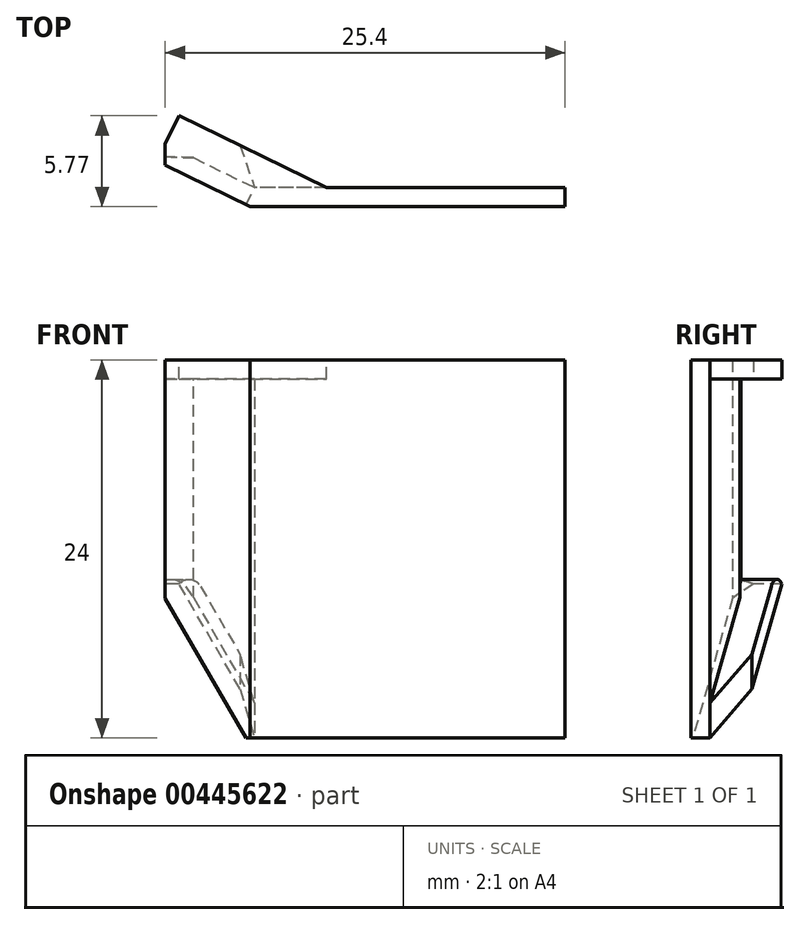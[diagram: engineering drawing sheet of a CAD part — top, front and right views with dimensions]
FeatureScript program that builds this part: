
annotation { "Feature Type Name" : "Feature", "Feature Type Description" : "" }
export const myFeature = defineFeature(function(context is Context, id is Id, definition is map)
    precondition{}
    {
        {
            var Q0;
            Q0=qCreatedBy(makeId("Top.planeOp"),FACE);
            var sketch = newSketch(context, id + "F0", { "sketchPlane" : qUnion([Q0])});
            skLineSegment(sketch, "E0", {"start": v(0, 0) * mm, "end": v(-20, 0) * mm});
            skLineSegment(sketch, "E1", {"start": v(-20, 0) * mm, "end": v(-25.4, 2.63) * mm});
            skLineSegment(sketch, "E2.0", {"start": v(-19.72, 1.2) * mm, "end": v(-25.4, 3.97) * mm});
            skLineSegment(sketch, "E2.1", {"start": v(0, 1.2) * mm, "end": v(-19.72, 1.2) * mm});
            skLineSegment(sketch, "E3", {"start": v(-25.4, 2.63) * mm, "end": v(-25.4, 3.97) * mm});
            skLineSegment(sketch, "E4", {"start": v(0, 0) * mm, "end": v(0, 1.2) * mm});
            skSolve(sketch);
        }
        {
            var Q0;
            Q0 = qSketchRegion(id + "F0", true);
            extrude(context, id + "F1", {"entities" : qUnion([Q0]), "depth" : 24 * mm});
        }
        {
            var Q0;
            Q0=makeQuery(id+"F1.opExtrude","SWEPT_FACE",FACE,{"disambiguationData":[OSD([sQuery(id+"F0.wireOp",EDGE,"E2.0")])]});
            var sketch = newSketch(context, id + "F2", { "sketchPlane" : qUnion([Q0])});
            skLineSegment(sketch, "E5", {"start": v(18.25, 0) * mm, "end": v(24.57, 9.79) * mm});
            skLineSegment(sketch, "E6", {"start": v(24.57, 9.79) * mm, "end": v(24.57, 12) * mm});
            skLineSegment(sketch, "E7", {"start": v(24.57, 12) * mm, "end": v(18.25, 2.21) * mm});
            skLineSegment(sketch, "E8", {"start": v(18.25, 2.21) * mm, "end": v(18.25, 0) * mm});
            skSolve(sketch);
        }
        {
            var Q0;
            Q0 = qSketchRegion(id + "F2", true);
            extrude(context, id + "F3", {"entities" : qUnion([Q0]), "operationType" : NewBodyOperationType.ADD, "depth" : 2 * mm});
        }
        {
            var Q0;
            Q0=makeQuery(id+"F3.opExtrude","CAP_EDGE",EDGE,{"disambiguationData":[OSD([sQuery(id+"F2.wireOp",EDGE,"E8")])],"isStart":false});
            chamfer(context, id + "F4", {"entities" : qUnion([Q0]), "width" : 2 * mm, "tangentPropagation" : true});
        }
        {
            var Q0;
            {var subQ2=sQuery(id+"F0.wireOp",EDGE,"E2.0");Q0=makeQuery(id+"F3.boolean.opBoolean","SPLIT",FACE,{"disambiguationData":[TD([makeQuery(id+"F3.opExtrude","SWEPT_FACE",FACE,{"disambiguationData":[OSD([sQuery(id+"F2.wireOp",EDGE,"E5")])]})])],"derivedFrom":makeQuery(id+"F1.opExtrude","SWEPT_FACE",FACE,{"disambiguationData":[OSD([subQ2])]})});}
            extrude(context, id + "F5", {"entities" : qUnion([Q0]), "operationType" : NewBodyOperationType.REMOVE, "oppositeDirection" : true, "depth" : 25 * mm});
        }
        {
            var Q0;
            Q0=makeQuery(id+"F1.opExtrude","CAP_FACE",FACE,{"disambiguationData":[OSD([sQuery(id+"F0.wireOp",EDGE,"E0"),sQuery(id+"F0.wireOp",EDGE,"E1"),sQuery(id+"F0.wireOp",EDGE,"E2.0"),sQuery(id+"F0.wireOp",EDGE,"E2.1"),sQuery(id+"F0.wireOp",EDGE,"E3"),sQuery(id+"F0.wireOp",EDGE,"E4")])],"isStart":false});
            var sketch = newSketch(context, id + "F6", { "sketchPlane" : qUnion([Q0])});
            skLineSegment(sketch, "E9", {"start": v(-25.4, 3.97) * mm, "end": v(-24.53, 5.77) * mm});
            skLineSegment(sketch, "E10", {"start": v(-24.53, 5.77) * mm, "end": v(-15.16, 1.2) * mm});
            skSolve(sketch);
        }
        {
            var Q0;
            Q0=makeQuery(id+"F6.imprint","IMPRINT",FACE,{"disambiguationData":[TD([[makeQuery(id+"F6.imprint","IMPRINT",EDGE,{"derivedFrom":sQuery(id+"F6.wireOp",EDGE,"E9")}),-1.0]])]});
            extrude(context, id + "F7", {"entities" : qUnion([Q0]), "operationType" : NewBodyOperationType.ADD, "oppositeDirection" : true, "depth" : 1.2 * mm});
        }
        {
            var Q0;
            {var subQ0=sQuery(id+"F0.wireOp",EDGE,"E2.0");var subQ1=sQuery(id+"F0.wireOp",EDGE,"E3");Q0=makeQuery(id+"F7.boolean.opBoolean","SPLIT",EDGE,{"derivedFrom":makeQuery(id+"F3.boolean.opBoolean","SPLIT",EDGE,{"disambiguationData":[TD([makeQuery(id+"F3.opExtrude","SWEPT_FACE",FACE,{"disambiguationData":[OSD([sQuery(id+"F2.wireOp",EDGE,"E7")])]})])],"derivedFrom":makeQuery(id+"F1.opExtrude","SWEPT_EDGE",EDGE,{"disambiguationData":[OSD([subQ0,subQ1])]})})});}
            chamfer(context, id + "F8", {"entities" : qUnion([Q0]), "chamferType" : ChamferType.TWO_OFFSETS, "width1" : 0.8 * mm, "oppositeDirection" : false, "width2" : 2 * mm, "tangentPropagation" : true});
        }
        {
            var Q0;
            Q0=makeQuery(id+"F3.opExtrude","SWEPT_EDGE",EDGE,{"disambiguationData":[OSD([sQuery(id+"F0.wireOp",EDGE,"E2.0"),sQuery(id+"F0.wireOp",EDGE,"E3"),sQuery(id+"F2.wireOp",EDGE,"E6"),sQuery(id+"F2.wireOp",EDGE,"E7")])]});
            fillet(context, id + "F9", {"entities" : qUnion([Q0]), "radius" : 1 * mm, "tangentPropagation" : true, "allowEdgeOverflow" : false});
        }
    });
